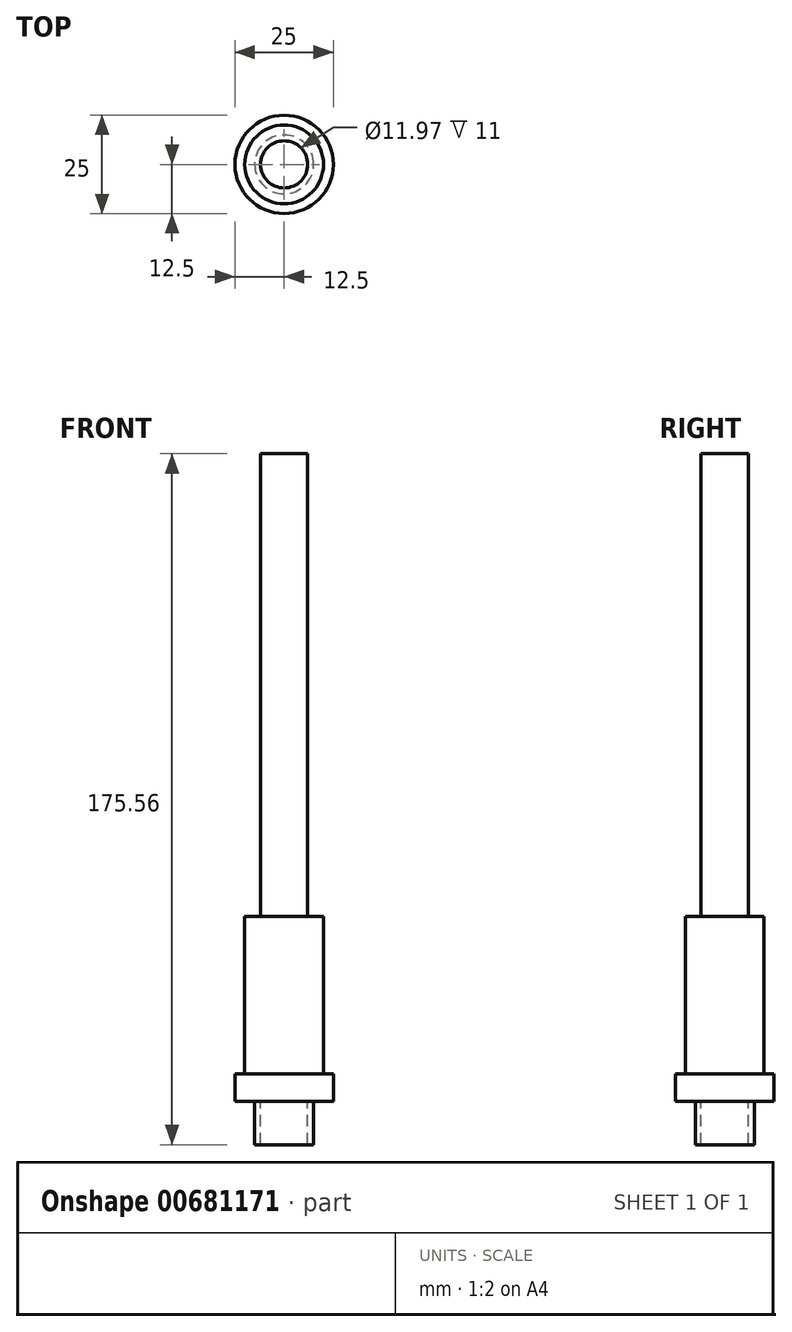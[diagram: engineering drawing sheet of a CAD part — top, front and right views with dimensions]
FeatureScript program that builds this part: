
annotation { "Feature Type Name" : "Feature", "Feature Type Description" : "" }
export const myFeature = defineFeature(function(context is Context, id is Id, definition is map)
    precondition{}
    {
        {
            var Q0;
            Q0=qCreatedBy(makeId("Top.planeOp"),FACE);
            var sketch = newSketch(context, id + "F0", { "sketchPlane" : qUnion([Q0])});
            skCircle(sketch, "E0", {"center": v(0, 0) * mm, "radius": 5.99 * mm});
            skCircle(sketch, "E1", {"center": v(0, 0) * mm, "radius": 7.49 * mm});
            skSolve(sketch);
        }
        {
            var Q0;
            Q0=makeQuery(id+"F0.imprint","IMPRINT",FACE,{"disambiguationData":[TD([[makeQuery(id+"F0.imprint","IMPRINT",EDGE,{"derivedFrom":sQuery(id+"F0.wireOp",EDGE,"E0")}),-1.0]])]});
            extrude(context, id + "F1", {"entities" : qUnion([Q0]), "oppositeDirection" : true, "depth" : 11 * mm, "offsetDistance" : 25 * mm});
        }
        {
            var Q0;
            Q0=makeQuery(id+"F1.opExtrude","CAP_FACE",FACE,{"disambiguationData":[OSD([sQuery(id+"F0.wireOp",EDGE,"E0"),sQuery(id+"F0.wireOp",EDGE,"E1")])],"isStart":true});
            var sketch = newSketch(context, id + "F2", { "sketchPlane" : qUnion([Q0])});
            skCircle(sketch, "E2", {"center": v(0, 0) * mm, "radius": 12.5 * mm});
            skSolve(sketch);
        }
        {
            var Q0;
            Q0=makeQuery(id+"F2.imprint","IMPRINT",FACE,{"disambiguationData":[TD([[makeQuery(id+"F2.imprint","IMPRINT",EDGE,{"derivedFrom":makeQuery(id+"F1.opExtrude","CAP_EDGE",EDGE,{"disambiguationData":[OSD([sQuery(id+"F0.wireOp",EDGE,"E0")])],"isStart":true})}),-1.0]])]});
            extrude(context, id + "F3", {"entities" : qUnion([Q0]), "operationType" : NewBodyOperationType.ADD, "depth" : 7 * mm, "offsetDistance" : 25 * mm});
        }
        {
            var Q0;
            Q0 = qSketchRegion(id + "F2", true);
            extrude(context, id + "F4", {"entities" : qUnion([Q0]), "operationType" : NewBodyOperationType.ADD, "depth" : 7 * mm, "offsetDistance" : 25 * mm});
        }
        {
            var Q0;
            Q0=makeQuery(id+"F4.boolean.opBoolean","MERGE",FACE,{"derivedFrom":[makeQuery(id+"F3.opExtrude","CAP_FACE",FACE,{"disambiguationData":[OSD([sQuery(id+"F0.wireOp",EDGE,"E0"),sQuery(id+"F0.wireOp",EDGE,"E1")])],"isStart":false}),makeQuery(id+"F4.opExtrude","CAP_FACE",FACE,{"disambiguationData":[OSD([sQuery(id+"F2.wireOp",EDGE,"E2")])],"isStart":false})]});
            var sketch = newSketch(context, id + "F5", { "sketchPlane" : qUnion([Q0])});
            skCircle(sketch, "E3", {"center": v(0, 0) * mm, "radius": 10 * mm});
            skSolve(sketch);
        }
        {
            var Q0;
            Q0=makeQuery(id+"F5.imprint","IMPRINT",FACE,{"disambiguationData":[TD([[makeQuery(id+"F5.imprint","IMPRINT",EDGE,{"derivedFrom":sQuery(id+"F5.wireOp",EDGE,"E3")}),1.0]])]});
            extrude(context, id + "F6", {"entities" : qUnion([Q0]), "operationType" : NewBodyOperationType.ADD, "depth" : 40.05 * mm, "offsetDistance" : 25 * mm});
        }
        {
            var Q0;
            Q0=makeQuery(id+"F6.opExtrude","CAP_FACE",FACE,{"disambiguationData":[OSD([sQuery(id+"F5.wireOp",EDGE,"E3")])],"isStart":false});
            var sketch = newSketch(context, id + "F7", { "sketchPlane" : qUnion([Q0])});
            skCircle(sketch, "E4", {"center": v(0, 0) * mm, "radius": 7.49 * mm});
            skSolve(sketch);
        }
        {
            var Q0;
            Q0=sQuery(id+"F7.wireOp",EDGE,"E4");
            extrude(context, id + "F8", {"bodyType" : ToolBodyType.SURFACE, "surfaceEntities" : qUnion([Q0]), "depth" : 54 * mm, "offsetDistance" : 25 * mm});
        }
        {
            var Q0;
            Q0=makeQuery(id+"F6.opExtrude","CAP_FACE",FACE,{"disambiguationData":[OSD([sQuery(id+"F5.wireOp",EDGE,"E3")])],"isStart":false});
            var sketch = newSketch(context, id + "F9", { "sketchPlane" : qUnion([Q0])});
            skCircle(sketch, "E5", {"center": v(0, 0) * mm, "radius": 5.99 * mm});
            skSolve(sketch);
        }
        {
            var Q0;
            Q0=makeQuery(id+"F9.imprint","IMPRINT",FACE,{"disambiguationData":[TD([[makeQuery(id+"F9.imprint","IMPRINT",EDGE,{"derivedFrom":sQuery(id+"F9.wireOp",EDGE,"E5")}),1.0]])]});
            extrude(context, id + "F10", {"entities" : qUnion([Q0]), "operationType" : NewBodyOperationType.ADD, "endBound" : BoundingType.THROUGH_ALL, "depth" : 25 * mm, "offsetDistance" : 25 * mm});
        }
    });
